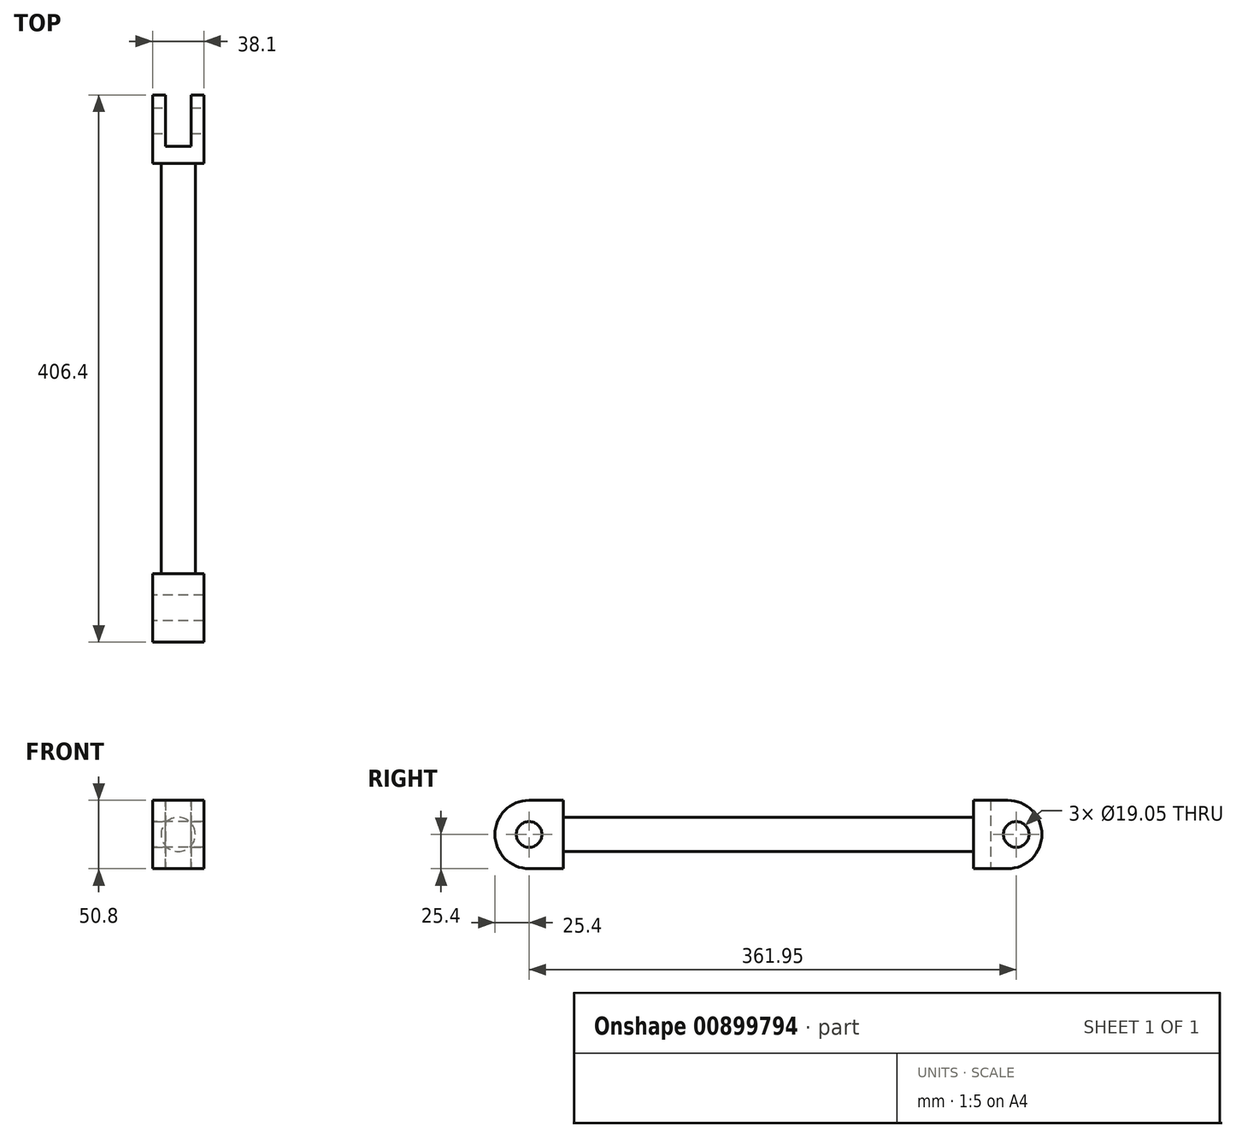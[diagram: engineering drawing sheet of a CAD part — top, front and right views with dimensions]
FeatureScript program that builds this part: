
annotation { "Feature Type Name" : "Feature", "Feature Type Description" : "" }
export const myFeature = defineFeature(function(context is Context, id is Id, definition is map)
    precondition{}
    {
        {
            var Q0;
            Q0=qCreatedBy(makeId("Front.planeOp"),FACE);
            var sketch = newSketch(context, id + "F0", { "sketchPlane" : qUnion([Q0])});
            skCircle(sketch, "E0", {"center": v(0, 0) * mm, "radius": 12.7 * mm});
            skSolve(sketch);
        }
        {
            var Q0;
            Q0 = qSketchRegion(id + "F0", true);
            extrude(context, id + "F1", {"entities" : qUnion([Q0]), "depth" : 304.8 * mm, "offsetDistance" : 25.4 * mm});
        }
        {
            var Q0;
            Q0=makeQuery(id+"F1.opExtrude","CAP_FACE",FACE,{"disambiguationData":[OSD([sQuery(id+"F0.wireOp",EDGE,"E0")])],"isStart":false});
            var sketch = newSketch(context, id + "F2", { "sketchPlane" : qUnion([Q0])});
            skLineSegment(sketch, "E1.bottom", {"start": v(19.05, 25.4) * mm, "end": v(-19.05, 25.4) * mm});
            skLineSegment(sketch, "E1.top", {"start": v(19.05, -25.4) * mm, "end": v(-19.05, -25.4) * mm});
            skLineSegment(sketch, "E1.left", {"start": v(19.05, 25.4) * mm, "end": v(19.05, -25.4) * mm});
            skLineSegment(sketch, "E1.right", {"start": v(-19.05, 25.4) * mm, "end": v(-19.05, -25.4) * mm});
            skPoint(sketch, "E1.middle", {"position": v(0, 0) * mm});
            skSolve(sketch);
        }
        {
            var Q0;
            Q0 = qSketchRegion(id + "F2", true);
            extrude(context, id + "F3", {"entities" : qUnion([Q0]), "operationType" : NewBodyOperationType.ADD, "depth" : 50.8 * mm, "offsetDistance" : 25.4 * mm});
        }
        {
            var Q0;
            Q0=makeQuery(id+"F3.opExtrude","SWEPT_FACE",FACE,{"disambiguationData":[OSD([sQuery(id+"F2.wireOp",EDGE,"E1.right")])]});
            var sketch = newSketch(context, id + "F4", { "sketchPlane" : qUnion([Q0])});
            skCircle(sketch, "E2", {"center": v(330.2, 0) * mm, "radius": 9.53 * mm});
            skPoint(sketch, "E2.centerSnap0", {"position": v(330.2, 25.4) * mm});
            skPoint(sketch, "E2.centerSnap1", {"position": v(355.6, 0) * mm});
            skSolve(sketch);
        }
        {
            var Q0;
            Q0 = qSketchRegion(id + "F4", true);
            extrude(context, id + "F5", {"entities" : qUnion([Q0]), "operationType" : NewBodyOperationType.REMOVE, "endBound" : BoundingType.THROUGH_ALL, "oppositeDirection" : true, "depth" : 25.4 * mm, "offsetDistance" : 25.4 * mm});
        }
        {
            var Q0;
            Q0=makeQuery(id+"F1.opExtrude","CAP_FACE",FACE,{"disambiguationData":[OSD([sQuery(id+"F0.wireOp",EDGE,"E0")])],"isStart":true});
            var sketch = newSketch(context, id + "F6", { "sketchPlane" : qUnion([Q0])});
            skLineSegment(sketch, "E3.bottom", {"start": v(19.05, 25.4) * mm, "end": v(-19.05, 25.4) * mm});
            skLineSegment(sketch, "E3.top", {"start": v(19.05, -25.4) * mm, "end": v(-19.05, -25.4) * mm});
            skLineSegment(sketch, "E3.left", {"start": v(19.05, 25.4) * mm, "end": v(19.05, -25.4) * mm});
            skLineSegment(sketch, "E3.right", {"start": v(-19.05, 25.4) * mm, "end": v(-19.05, -25.4) * mm});
            skPoint(sketch, "E3.middle", {"position": v(0, 0) * mm});
            skSolve(sketch);
        }
        {
            var Q0;
            Q0 = qSketchRegion(id + "F6", true);
            extrude(context, id + "F7", {"entities" : qUnion([Q0]), "operationType" : NewBodyOperationType.ADD, "depth" : 50.8 * mm, "offsetDistance" : 25.4 * mm});
        }
        {
            var Q0;
            Q0=makeQuery(id+"F7.opExtrude","CAP_FACE",FACE,{"disambiguationData":[OSD([sQuery(id+"F6.wireOp",EDGE,"E3.bottom"),sQuery(id+"F6.wireOp",EDGE,"E3.top"),sQuery(id+"F6.wireOp",EDGE,"E3.left"),sQuery(id+"F6.wireOp",EDGE,"E3.right")])],"isStart":false});
            var sketch = newSketch(context, id + "F8", { "sketchPlane" : qUnion([Q0])});
            skLineSegment(sketch, "E4.bottom", {"start": v(9.53, 25.4) * mm, "end": v(-9.53, 25.4) * mm});
            skLineSegment(sketch, "E4.top", {"start": v(9.53, -25.4) * mm, "end": v(-9.53, -25.4) * mm});
            skLineSegment(sketch, "E4.left", {"start": v(9.53, 25.4) * mm, "end": v(9.53, -25.4) * mm});
            skLineSegment(sketch, "E4.right", {"start": v(-9.53, 25.4) * mm, "end": v(-9.53, -25.4) * mm});
            skPoint(sketch, "E4.middle", {"position": v(0, 0) * mm});
            skSolve(sketch);
        }
        {
            var Q0;
            Q0 = qSketchRegion(id + "F8", true);
            extrude(context, id + "F9", {"entities" : qUnion([Q0]), "operationType" : NewBodyOperationType.REMOVE, "oppositeDirection" : true, "depth" : 38.1 * mm, "offsetDistance" : 25.4 * mm});
        }
        {
            var Q0;
            Q0=makeQuery(id+"F7.opExtrude","SWEPT_FACE",FACE,{"disambiguationData":[OSD([sQuery(id+"F6.wireOp",EDGE,"E3.right")])]});
            var sketch = newSketch(context, id + "F10", { "sketchPlane" : qUnion([Q0])});
            skCircle(sketch, "E5", {"center": v(31.75, 0) * mm, "radius": 9.53 * mm});
            skPoint(sketch, "E5.centerSnap0", {"position": v(50.8, 0) * mm});
            skSolve(sketch);
        }
        {
            var Q0;
            Q0 = qSketchRegion(id + "F10", true);
            extrude(context, id + "F11", {"entities" : qUnion([Q0]), "operationType" : NewBodyOperationType.REMOVE, "endBound" : BoundingType.THROUGH_ALL, "oppositeDirection" : true, "depth" : 25.4 * mm, "offsetDistance" : 25.4 * mm});
        }
        {
            var Q0;
            {var subQ0=sQuery(id+"F6.wireOp",EDGE,"E3.bottom");var subQ1=sQuery(id+"F6.wireOp",EDGE,"E3.right");Q0=makeQuery(id+"F9.boolean.opBoolean","SPLIT",EDGE,{"disambiguationData":[TD([makeQuery(id+"F7.opExtrude","SWEPT_FACE",FACE,{"disambiguationData":[OSD([subQ1])]})])],"derivedFrom":makeQuery(id+"F7.opExtrude","CAP_EDGE",EDGE,{"disambiguationData":[OSD([subQ0])],"isStart":false})});}
            var Q1;
            {var subQ0=sQuery(id+"F6.wireOp",EDGE,"E3.right");var subQ1=sQuery(id+"F6.wireOp",EDGE,"E3.top");Q1=makeQuery(id+"F9.boolean.opBoolean","SPLIT",EDGE,{"disambiguationData":[TD([makeQuery(id+"F7.opExtrude","SWEPT_FACE",FACE,{"disambiguationData":[OSD([subQ0])]})])],"derivedFrom":makeQuery(id+"F7.opExtrude","CAP_EDGE",EDGE,{"disambiguationData":[OSD([subQ1])],"isStart":false})});}
            var Q2;
            {var subQ0=sQuery(id+"F6.wireOp",EDGE,"E3.left");var subQ1=sQuery(id+"F6.wireOp",EDGE,"E3.top");Q2=makeQuery(id+"F9.boolean.opBoolean","SPLIT",EDGE,{"disambiguationData":[TD([makeQuery(id+"F7.opExtrude","SWEPT_FACE",FACE,{"disambiguationData":[OSD([subQ0])]})])],"derivedFrom":makeQuery(id+"F7.opExtrude","CAP_EDGE",EDGE,{"disambiguationData":[OSD([subQ1])],"isStart":false})});}
            var Q3;
            {var subQ0=sQuery(id+"F6.wireOp",EDGE,"E3.bottom");var subQ1=sQuery(id+"F6.wireOp",EDGE,"E3.left");Q3=makeQuery(id+"F9.boolean.opBoolean","SPLIT",EDGE,{"disambiguationData":[TD([makeQuery(id+"F7.opExtrude","SWEPT_FACE",FACE,{"disambiguationData":[OSD([subQ1])]})])],"derivedFrom":makeQuery(id+"F7.opExtrude","CAP_EDGE",EDGE,{"disambiguationData":[OSD([subQ0])],"isStart":false})});}
            var Q4;
            Q4=makeQuery(id+"F3.opExtrude","CAP_EDGE",EDGE,{"disambiguationData":[OSD([sQuery(id+"F2.wireOp",EDGE,"E1.bottom")])],"isStart":false});
            var Q5;
            Q5=makeQuery(id+"F3.opExtrude","CAP_EDGE",EDGE,{"disambiguationData":[OSD([sQuery(id+"F2.wireOp",EDGE,"E1.top")])],"isStart":false});
            fillet(context, id + "F12", {"entities" : qUnion([Q0, Q1, Q2, Q3, Q4, Q5]), "radius" : 25.4 * mm, "tangentPropagation" : true, "allowEdgeOverflow" : false});
        }
    });
